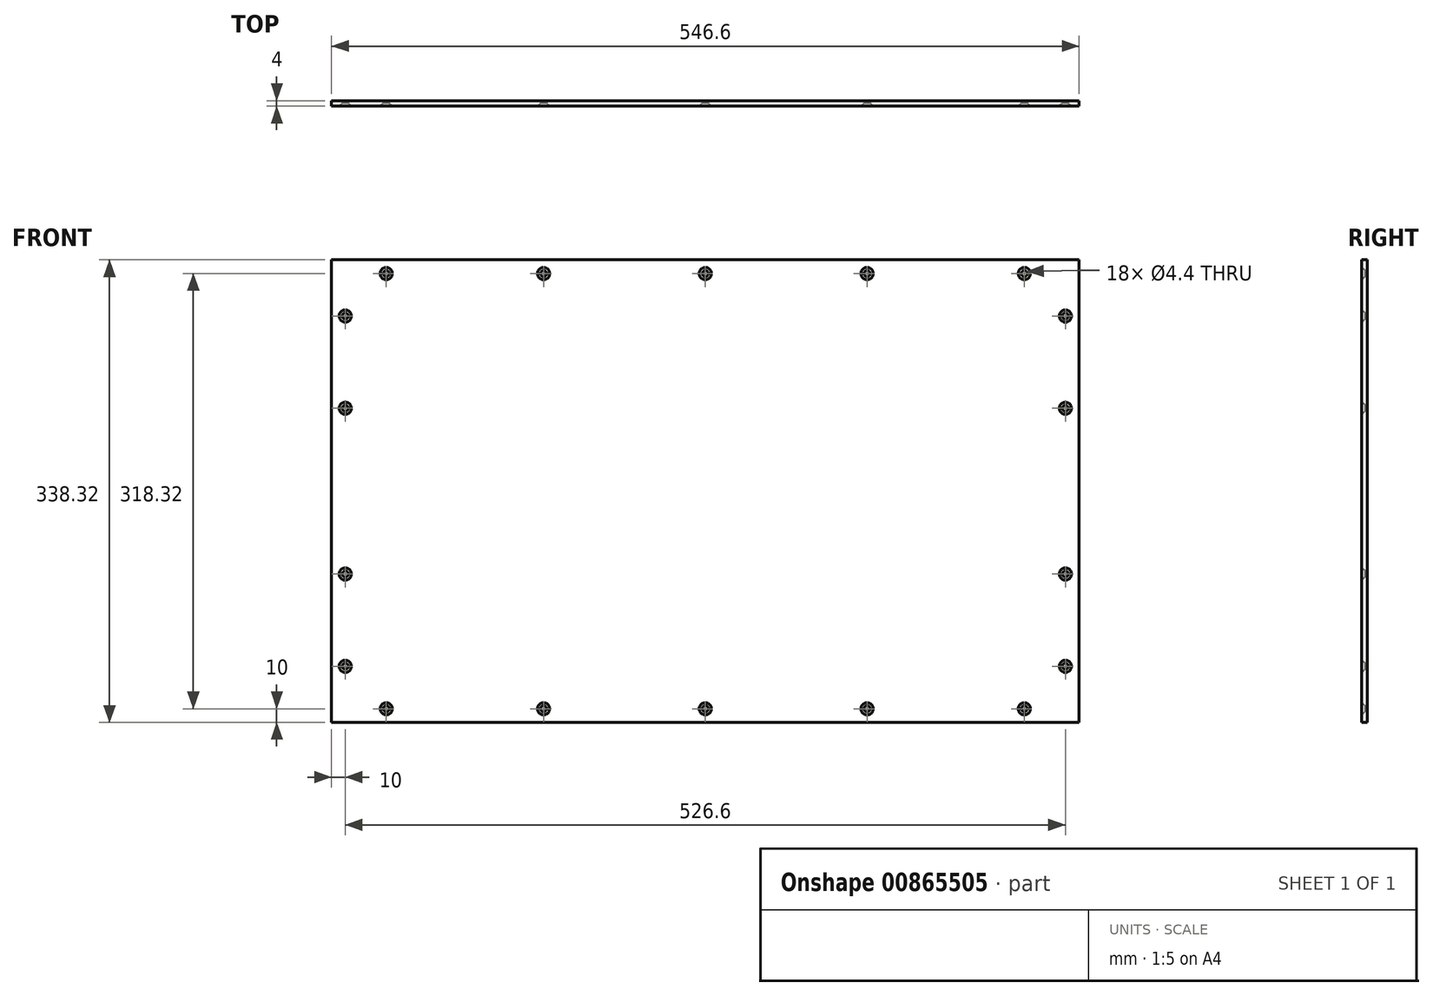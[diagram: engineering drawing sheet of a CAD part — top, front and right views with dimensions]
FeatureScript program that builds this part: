
annotation { "Feature Type Name" : "Feature", "Feature Type Description" : "" }
export const myFeature = defineFeature(function(context is Context, id is Id, definition is map)
    precondition{}
    {
        {
            var Q0;
            Q0=qCreatedBy(makeId("Front.planeOp"),FACE);
            var sketch = newSketch(context, id + "F0", { "sketchPlane" : qUnion([Q0])});
            skLineSegment(sketch, "E0.bottom", {"start": v(0, 0) * mm, "end": v(546.6, 0) * mm});
            skLineSegment(sketch, "E0.top", {"start": v(0, 299.2) * mm, "end": v(546.6, 299.2) * mm});
            skLineSegment(sketch, "E0.left", {"start": v(0, 0) * mm, "end": v(0, 299.2) * mm});
            skLineSegment(sketch, "E0.right", {"start": v(546.6, 0) * mm, "end": v(546.6, 299.2) * mm});
            skLineSegment(sketch, "E1", {"start": v(25.05, 295.7) * mm, "end": v(25.05, 3.5) * mm});
            skLineSegment(sketch, "E2", {"start": v(521.55, 295.7) * mm, "end": v(521.55, 3.5) * mm});
            skLineSegment(sketch, "E3", {"start": v(526.6, 299.2) * mm, "end": v(526.6, 0) * mm});
            skLineSegment(sketch, "E4", {"start": v(20, 299.2) * mm, "end": v(20, 0) * mm});
            skLineSegment(sketch, "E5", {"start": v(25.05, 295.7) * mm, "end": v(521.55, 295.7) * mm});
            skLineSegment(sketch, "E6", {"start": v(25.05, 3.5) * mm, "end": v(521.55, 3.5) * mm});
            skLineSegment(sketch, "E7.bottom", {"start": v(35.27, 283.49) * mm, "end": v(511.33, 283.5) * mm});
            skLineSegment(sketch, "E7.top", {"start": v(35.27, 15.71) * mm, "end": v(511.33, 15.71) * mm});
            skLineSegment(sketch, "E7.left", {"start": v(35.27, 283.49) * mm, "end": v(35.27, 15.71) * mm});
            skLineSegment(sketch, "E7.right", {"start": v(511.33, 283.5) * mm, "end": v(511.33, 15.71) * mm});
            skLineSegment(sketch, "E8", {"start": v(273.3, 283.5) * mm, "end": v(273.3, 15.71) * mm, "construction": true});
            skLineSegment(sketch, "E9", {"start": v(536.6, 299.2) * mm, "end": v(536.6, 0) * mm, "construction": true});
            skLineSegment(sketch, "E10", {"start": v(0, 149.6) * mm, "end": v(546.6, 149.6) * mm, "construction": true});
            skArc(sketch, "E11", {"start": v(539.1, 280.2) * mm, "mid": v(536.6, 282.7) * mm, "end": v(534.1, 280.2) * mm});
            skArc(sketch, "E12", {"start": v(534.1, 275.2) * mm, "mid": v(536.6, 272.7) * mm, "end": v(539.1, 275.2) * mm});
            skLineSegment(sketch, "E13", {"start": v(534.1, 280.2) * mm, "end": v(534.1, 275.2) * mm});
            skLineSegment(sketch, "E14", {"start": v(539.1, 280.2) * mm, "end": v(539.1, 275.2) * mm});
            skLineSegment(sketch, "E15", {"start": v(534.1, 210.2) * mm, "end": v(539.1, 210.2) * mm, "construction": true});
            skArc(sketch, "E16", {"start": v(534.1, 212.7) * mm, "mid": v(531.6, 210.2) * mm, "end": v(534.1, 207.7) * mm});
            skArc(sketch, "E17", {"start": v(539.1, 207.7) * mm, "mid": v(541.6, 210.2) * mm, "end": v(539.1, 212.7) * mm});
            skLineSegment(sketch, "E18", {"start": v(534.1, 212.7) * mm, "end": v(539.1, 212.7) * mm});
            skLineSegment(sketch, "E19", {"start": v(534.1, 207.7) * mm, "end": v(539.1, 207.7) * mm});
            skLineSegment(sketch, "E20.MirrorCS", {"start": v(539.1, 19) * mm, "end": v(539.1, 24) * mm});
            skArc(sketch, "E21.MirrorCS", {"start": v(539.1, 19) * mm, "mid": v(536.6, 16.5) * mm, "end": v(534.1, 19) * mm});
            skLineSegment(sketch, "E22.MirrorCS", {"start": v(534.1, 19) * mm, "end": v(534.1, 24) * mm});
            skArc(sketch, "E23.MirrorCS", {"start": v(534.1, 24) * mm, "mid": v(536.6, 26.5) * mm, "end": v(539.1, 24) * mm});
            skLineSegment(sketch, "E24.MirrorCS", {"start": v(534.1, 91.5) * mm, "end": v(539.1, 91.5) * mm});
            skArc(sketch, "E25.MirrorCS", {"start": v(539.1, 91.5) * mm, "mid": v(541.6, 89) * mm, "end": v(539.1, 86.5) * mm});
            skLineSegment(sketch, "E26.MirrorCS", {"start": v(534.1, 86.5) * mm, "end": v(539.1, 86.5) * mm});
            skArc(sketch, "E27.MirrorCS", {"start": v(534.1, 86.5) * mm, "mid": v(531.6, 89) * mm, "end": v(534.1, 91.5) * mm});
            skLineSegment(sketch, "E28.MirrorCS", {"start": v(10, 299.2) * mm, "end": v(10, 0) * mm, "construction": true});
            skLineSegment(sketch, "E29.MirrorCS", {"start": v(7.5, 280.2) * mm, "end": v(7.5, 275.2) * mm});
            skLineSegment(sketch, "E30.MirrorCS", {"start": v(12.5, 280.2) * mm, "end": v(12.5, 275.2) * mm});
            skArc(sketch, "E31.MirrorCS", {"start": v(7.5, 280.2) * mm, "mid": v(10, 282.7) * mm, "end": v(12.5, 280.2) * mm});
            skArc(sketch, "E32.MirrorCS", {"start": v(12.5, 275.2) * mm, "mid": v(10, 272.7) * mm, "end": v(7.5, 275.2) * mm});
            skLineSegment(sketch, "E33.MirrorCS", {"start": v(12.5, 207.7) * mm, "end": v(7.5, 207.7) * mm});
            skLineSegment(sketch, "E34.MirrorCS", {"start": v(12.5, 212.7) * mm, "end": v(7.5, 212.7) * mm});
            skArc(sketch, "E35.MirrorCS", {"start": v(7.5, 207.7) * mm, "mid": v(5, 210.2) * mm, "end": v(7.5, 212.7) * mm});
            skArc(sketch, "E36.MirrorCS", {"start": v(12.5, 212.7) * mm, "mid": v(15, 210.2) * mm, "end": v(12.5, 207.7) * mm});
            skLineSegment(sketch, "E37.MirrorCS", {"start": v(12.5, 86.5) * mm, "end": v(7.5, 86.5) * mm});
            skLineSegment(sketch, "E38.MirrorCS", {"start": v(12.5, 91.5) * mm, "end": v(7.5, 91.5) * mm});
            skArc(sketch, "E39.MirrorCS", {"start": v(7.5, 91.5) * mm, "mid": v(5, 89) * mm, "end": v(7.5, 86.5) * mm});
            skArc(sketch, "E40.MirrorCS", {"start": v(12.5, 86.5) * mm, "mid": v(15, 89) * mm, "end": v(12.5, 91.5) * mm});
            skArc(sketch, "E41.MirrorCS", {"start": v(12.5, 24) * mm, "mid": v(10, 26.5) * mm, "end": v(7.5, 24) * mm});
            skLineSegment(sketch, "E42.MirrorCS", {"start": v(7.5, 19) * mm, "end": v(7.5, 24) * mm});
            skLineSegment(sketch, "E43.MirrorCS", {"start": v(12.5, 19) * mm, "end": v(12.5, 24) * mm});
            skArc(sketch, "E44.MirrorCS", {"start": v(7.5, 19) * mm, "mid": v(10, 16.5) * mm, "end": v(12.5, 19) * mm});
            skLineSegment(sketch, "E45", {"start": v(7.5, 277.7) * mm, "end": v(12.5, 277.7) * mm, "construction": true});
            skLineSegment(sketch, "E46", {"start": v(7.5, 210.2) * mm, "end": v(12.5, 210.2) * mm, "construction": true});
            skLineSegment(sketch, "E47", {"start": v(7.5, 89) * mm, "end": v(12.5, 89) * mm, "construction": true});
            skLineSegment(sketch, "E48", {"start": v(7.5, 21.5) * mm, "end": v(12.5, 21.5) * mm, "construction": true});
            skPoint(sketch, "E49", {"position": v(10, 21.5) * mm});
            skPoint(sketch, "E50", {"position": v(10, 89) * mm});
            skPoint(sketch, "E51", {"position": v(10, 210.2) * mm});
            skPoint(sketch, "E52", {"position": v(10, 277.7) * mm});
            skLineSegment(sketch, "E53", {"start": v(534.1, 277.7) * mm, "end": v(539.1, 277.7) * mm, "construction": true});
            skLineSegment(sketch, "E54", {"start": v(534.1, 89) * mm, "end": v(539.1, 89) * mm, "construction": true});
            skLineSegment(sketch, "E55", {"start": v(534.1, 21.5) * mm, "end": v(539.1, 21.5) * mm, "construction": true});
            skPoint(sketch, "E56", {"position": v(536.6, 21.5) * mm});
            skPoint(sketch, "E57", {"position": v(536.6, 89) * mm});
            skPoint(sketch, "E58", {"position": v(536.6, 210.2) * mm});
            skPoint(sketch, "E59", {"position": v(536.6, 277.7) * mm});
            skSolve(sketch);
        }
        {
            var Q0;
            Q0=qCreatedBy(makeId("Front.planeOp"),FACE);
            var sketch = newSketch(context, id + "F1", { "sketchPlane" : qUnion([Q0])});
            skLineSegment(sketch, "E60", {"start": v(0, 318.76) * mm, "end": v(0, -19.56) * mm});
            skLineSegment(sketch, "E61", {"start": v(0, -19.56) * mm, "end": v(546.6, -19.56) * mm});
            skLineSegment(sketch, "E62", {"start": v(546.6, -19.56) * mm, "end": v(546.6, 318.76) * mm});
            skLineSegment(sketch, "E63", {"start": v(546.6, 318.76) * mm, "end": v(0, 318.76) * mm});
            skLineSegment(sketch, "E64.bottom", {"start": v(34, 284.76) * mm, "end": v(512.6, 284.76) * mm});
            skLineSegment(sketch, "E64.top", {"start": v(34, 14.44) * mm, "end": v(512.6, 14.44) * mm});
            skLineSegment(sketch, "E64.left", {"start": v(34, 284.76) * mm, "end": v(34, 14.44) * mm});
            skLineSegment(sketch, "E64.right", {"start": v(512.6, 284.76) * mm, "end": v(512.6, 14.44) * mm});
            skLineSegment(sketch, "E65", {"start": v(0, 308.76) * mm, "end": v(546.6, 308.76) * mm, "construction": true});
            skLineSegment(sketch, "E66", {"start": v(0, -9.56) * mm, "end": v(546.6, -9.56) * mm, "construction": true});
            skPoint(sketch, "E67", {"position": v(40, 308.76) * mm});
            skPoint(sketch, "E68", {"position": v(506.6, 308.76) * mm});
            skPoint(sketch, "E69", {"position": v(273.3, 308.76) * mm});
            skPoint(sketch, "E70", {"position": v(155, 308.76) * mm});
            skPoint(sketch, "E71", {"position": v(391.6, 308.76) * mm});
            skPoint(sketch, "E72.MirrorP", {"position": v(40, -9.56) * mm});
            skPoint(sketch, "E73.MirrorP", {"position": v(155, -9.56) * mm});
            skPoint(sketch, "E74.MirrorP", {"position": v(273.3, -9.56) * mm});
            skPoint(sketch, "E75.MirrorP", {"position": v(391.6, -9.56) * mm});
            skPoint(sketch, "E76.MirrorP", {"position": v(506.6, -9.56) * mm});
            skSolve(sketch);
        }
        {
            var Q0;
            Q0=makeQuery(id+"F1.imprint","IMPRINT",FACE,{"disambiguationData":[TD([[makeQuery(id+"F1.imprint","IMPRINT",EDGE,{"derivedFrom":sQuery(id+"F1.wireOp",EDGE,"E60")}),1.0]])]});
            var Q1;
            Q1=makeQuery(id+"F1.imprint","IMPRINT",FACE,{"disambiguationData":[TD([[makeQuery(id+"F1.imprint","IMPRINT",EDGE,{"derivedFrom":sQuery(id+"F1.wireOp",EDGE,"E64.bottom")}),-1.0]])]});
            extrude(context, id + "F2", {"entities" : qUnion([Q0, Q1]), "oppositeDirection" : true, "depth" : 4 * mm, "offsetDistance" : 25 * mm});
        }
        {
            var Q0;
            Q0=sQuery(id+"F0.wireOp",VERTEX,"E52");
            var Q1;
            Q1=sQuery(id+"F1.wireOp",VERTEX,"E67");
            var Q2;
            Q2=sQuery(id+"F1.wireOp",VERTEX,"E70");
            var Q3;
            Q3=sQuery(id+"F1.wireOp",VERTEX,"E69");
            var Q4;
            Q4=sQuery(id+"F1.wireOp",VERTEX,"E71");
            var Q5;
            Q5=sQuery(id+"F1.wireOp",VERTEX,"E68");
            var Q6;
            Q6=sQuery(id+"F0.wireOp",VERTEX,"E51");
            var Q7;
            Q7=sQuery(id+"F0.wireOp",VERTEX,"E50");
            var Q8;
            Q8=sQuery(id+"F0.wireOp",VERTEX,"E49");
            var Q9;
            Q9=sQuery(id+"F1.wireOp",VERTEX,"E72.MirrorP");
            var Q10;
            Q10=sQuery(id+"F1.wireOp",VERTEX,"E73.MirrorP");
            var Q11;
            Q11=sQuery(id+"F1.wireOp",VERTEX,"E74.MirrorP");
            var Q12;
            Q12=sQuery(id+"F1.wireOp",VERTEX,"E75.MirrorP");
            var Q13;
            Q13=sQuery(id+"F1.wireOp",VERTEX,"E76.MirrorP");
            var Q14;
            Q14=sQuery(id+"F0.wireOp",VERTEX,"E56");
            var Q15;
            Q15=sQuery(id+"F0.wireOp",VERTEX,"E57");
            var Q16;
            Q16=sQuery(id+"F0.wireOp",VERTEX,"E58");
            var Q17;
            Q17=sQuery(id+"F0.wireOp",VERTEX,"E59");
            var Q18;
            Q18=makeQuery(id+"F2.opExtrude","SWEPT_BODY",BODY,{"disambiguationData":[OSD([sQuery(id+"F1.wireOp",EDGE,"E60"),sQuery(id+"F1.wireOp",EDGE,"E61"),sQuery(id+"F1.wireOp",EDGE,"E62"),sQuery(id+"F1.wireOp",EDGE,"E63"),sQuery(id+"F1.wireOp",EDGE,"E64.bottom"),sQuery(id+"F1.wireOp",EDGE,"E64.top"),sQuery(id+"F1.wireOp",EDGE,"E64.left"),sQuery(id+"F1.wireOp",EDGE,"E64.right")])]});
            hole(context, id + "F3", {"style" : HoleStyle.C_SINK, "endStyle" : HoleEndStyle.THROUGH, "standardTappedOrClearance" : lookupTablePath({ "fit" : "Normal", "standard" : "ISO", "size" : "M4", "type" : "Clearance" }), "standardBlindInLast" : lookupTablePath({ "fit" : "Standard", "standard" : "ISO", "size" : "M4", "type" : "Clearance" }), "holeDiameter" : 4.4 * mm, "cSinkDiameter" : 8.96 * mm, "cSinkAngle" : 90 * degree, "majorDiameter" : 5 * mm, "isTappedThrough" : true, "tappedDepth" : 12 * mm, "tapClearance" : 3, "locations" : qUnion([Q0, Q1, Q2, Q3, Q4, Q5, Q6, Q7, Q8, Q9, Q10, Q11, Q12, Q13, Q14, Q15, Q16, Q17]), "scope" : qUnion([Q18])});
        }
    });
